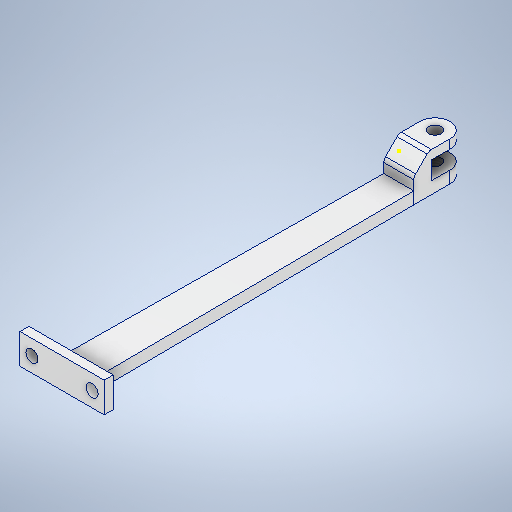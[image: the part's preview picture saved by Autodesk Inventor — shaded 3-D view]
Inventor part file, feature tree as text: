
AUTODESK INVENTOR PART (.ipt)
format: ipt  version: 2025.1 (Build 291241000, 241)  size: 334,336 bytes
history: native  units: mm
features: sketch x7, fillet x4, extrude x3, hole x3
ambient origin geometry x8: Origin, YZ Plane, XZ Plane, XY Plane, X Axis, Y Axis, Z Axis, Center Point
bodies: Volumenkörper1 (feature_tree)
feature tree (17):
  sketch  "Skizze1"  dims[d0=17.0mm d1=13.0mm d2=5.0mm d3=12.0mm d4=11.0mm]
  extrude  "Extrusion1"  Depth=5.0mm
  fillet  "Rundung1"  Radius=12.0mm
  fillet  "Rundung2"  Radius=11.0mm
  hole  "Bohrung1"  [1 undecoded]
  hole  "Bohrung2"  [1 undecoded]
  extrude  "Extrusion2"  Depth=10.0mm TaperAngle=0.0deg
  fillet  "Rundung3"  Radius=5.0mm
  extrude  "Extrusion3"  Depth=10.0mm
  fillet  "Rundung4"  Radius=121.0mm
  hole  "Bohrung3"  [1 undecoded]
  sketch  "Skizze2"  dims[d5=3.0mm d6=4.0mm]
  sketch  "Skizze4"  dims[d7=11.0mm d8=12.0mm]
  sketch  "Skizze5"  dims[d9=17.0mm d10=10.0mm d11=0.0mm d13=5.0mm]
  sketch  "Skizze6"  dims[d14=5.0mm]
  sketch  "Skizze7"  dims[d15=4.134mm d16=10.0mm d17=4.0mm d18=2.0mm d19=90.0deg d20=8.0mm d21=0.0mm]
  sketch  "Skizze8"  dims[d22=4.134mm d23=10.0mm d24=4.0mm d25=2.0mm d26=90.0deg d27=8.0mm d28=0.0mm d29=12.0mm d30=121.0mm d31=4.0mm d32=0.0mm d33=2.0mm d34=28.0mm d35=3.0mm d36=10.0mm d37=0.0mm d38=0.5mm d39=4.0mm d40=8.0mm d41=4.0mm d42=2.0mm d43=90.0deg d44=8.0mm d45=0.0mm d46=10.0mm d47=10.0mm]
note: 3 required parameter values undecoded (feature->parameter linkage not recoverable at this tier; creation-order binding heuristic only, values carry confidence <= 0.55)
